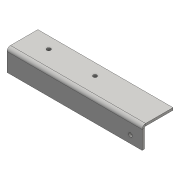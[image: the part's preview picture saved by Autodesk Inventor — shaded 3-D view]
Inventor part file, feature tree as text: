
AUTODESK INVENTOR PART (.ipt)
format: ipt  version: 2016 (Build 200138000, 138)  size: 146,432 bytes
history: native  units: mm
features: other x4, sheet_metal_op x3, hole x3, sketch x2
ambient origin geometry x8: Origin, YZ Plane, XZ Plane, XY Plane, X Axis, Y Axis, Z Axis, Center Point
bodies: Solid1 (feature_tree)
feature tree (12):
  other  "endcapOptionRightAngle"
  sheet_metal_op  "Face1"
  sheet_metal_op  "Face2"
  hole  "Hole1"  [1 undecoded]
  hole  "Hole2"  [1 undecoded]
  hole  "Hole3"  [1 undecoded]
  sketch  "Sketch1"  dims[d0=175.0mm d1=40.0mm]
  other  "Plate1"
  sketch  "Sketch2"  dims[d2=3.0mm d3=25.0mm d4=175.0mm d5=1.5mm d6=3.0mm d7=1.5mm d8=6.0mm d9=3.0mm d10=29.0mm d11=15.0mm d12=5.0mm d13=6.0mm d14=4.0mm d15=2.0mm d16=90.0deg d17=3.0mm d18=20.594885mm d19=89.0mm d20=15.0mm d21=5.0mm d22=6.0mm d23=4.0mm d24=2.0mm d25=90.0deg d26=3.0mm d27=20.594885mm d28=15.0mm d29=10.0mm d30=5.0mm d31=6.0mm d32=4.0mm d33=2.0mm d34=90.0deg d35=3.0mm d36=20.594885mm]
  other  "Plate2"
  sheet_metal_op  "Bend1"
  other  "Definition1"
note: 3 required parameter values undecoded (feature->parameter linkage not recoverable at this tier; creation-order binding heuristic only, values carry confidence <= 0.55)
